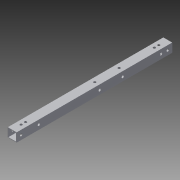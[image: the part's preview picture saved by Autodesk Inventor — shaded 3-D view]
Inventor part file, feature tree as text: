
AUTODESK INVENTOR PART (.ipt)
format: ipt  version: 2013 (Build 170138000, 138)  size: 128,512 bytes
history: native  units: in
note: dims shown in document units (in); Inventor stores cm internally (conversion verified against a paired STEP export)
features: extrude x6, sketch x5
ambient origin geometry x8: Origin, YZ Plane, XZ Plane, XY Plane, X Axis, Y Axis, Z Axis, Center Point
bodies: Solid1 (feature_tree)
feature tree (11):
  extrude  "Extrusion1"  Depth=1.0in
  extrude  "Extrusion2"  Depth=20.0in TaperAngle=0.0deg
  extrude  "Extrusion3"  Depth=0.1321in
  extrude  "Extrusion4"  Depth=1.0in TaperAngle=0.0deg
  extrude  "Extrusion13"  Depth=1.0in TaperAngle=0.0deg
  extrude  "Extrusion14"  Depth=1.0in TaperAngle=0.0deg
  sketch  "Sketch1"  dims[d0=1.0in d2=1.0in]
  sketch  "Sketch3"  dims[d3=0.0625in d4=20.0in d5=0.0in]
  sketch  "Sketch4"  dims[d9=20.0in d10=0.0in d12=0.1321in]
  sketch  "Sketch13"  dims[d13=17.5in d14=1.0in d15=0.0in]
  sketch  "Sketch14"  dims[d16=1.0in d17=0.0in d34=1.0in d35=0.0in d36=1.0in d37=0.0in]
